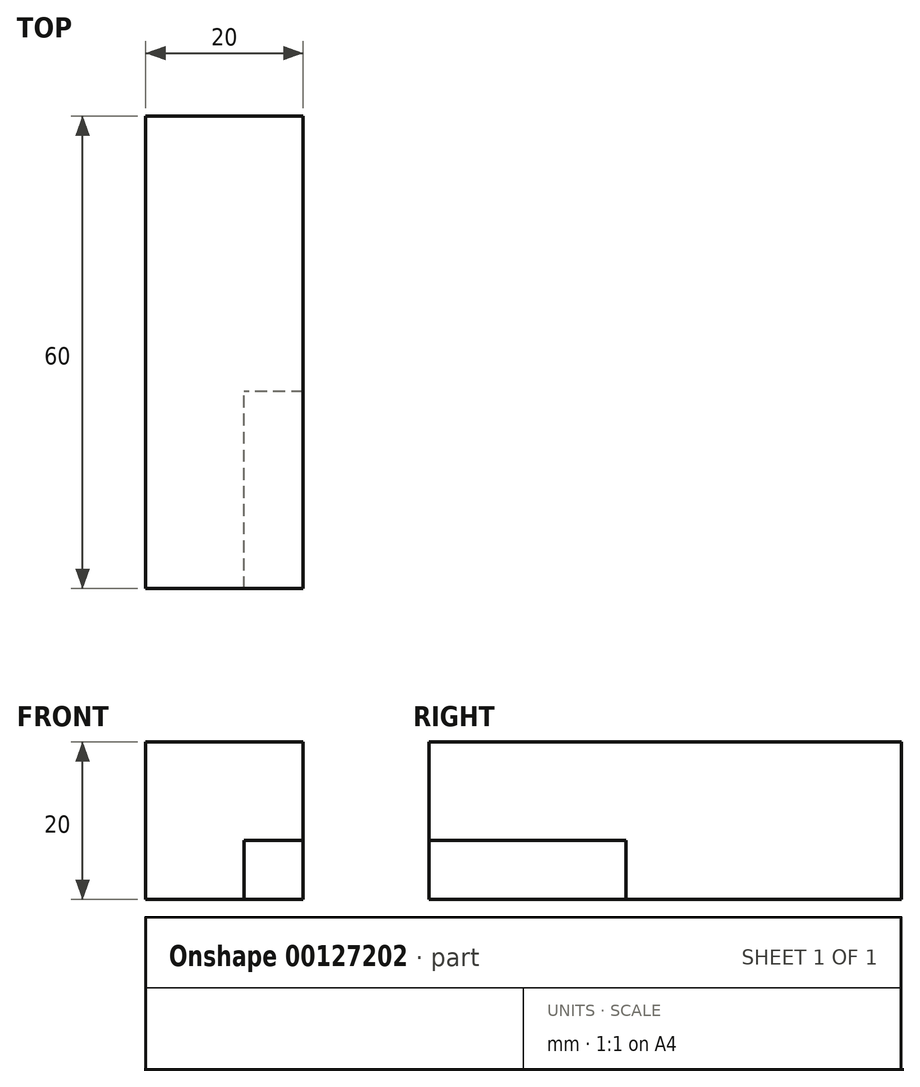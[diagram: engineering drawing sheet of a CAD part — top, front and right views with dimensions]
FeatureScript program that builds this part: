
annotation { "Feature Type Name" : "Feature", "Feature Type Description" : "" }
export const myFeature = defineFeature(function(context is Context, id is Id, definition is map)
    precondition{}
    {
        {
            var Q0;
            Q0=qCreatedBy(makeId("Front.planeOp"),FACE);
            var sketch = newSketch(context, id + "F0", { "sketchPlane" : qUnion([Q0])});
            skLineSegment(sketch, "E0.bottom", {"start": v(-7.5, 0) * mm, "end": v(-20, 0) * mm});
            skLineSegment(sketch, "E0.top", {"start": v(0, 20) * mm, "end": v(-20, 20) * mm});
            skLineSegment(sketch, "E0.left", {"start": v(0, 7.5) * mm, "end": v(0, 20) * mm});
            skLineSegment(sketch, "E0.right", {"start": v(-20, 0) * mm, "end": v(-20, 20) * mm});
            skLineSegment(sketch, "E1.top", {"start": v(0, 7.5) * mm, "end": v(-7.5, 7.5) * mm});
            skLineSegment(sketch, "E1.right", {"start": v(-7.5, 0) * mm, "end": v(-7.5, 7.5) * mm});
            skSolve(sketch);
        }
        {
            var Q0;
            Q0 = qSketchRegion(id + "F0", true);
            extrude(context, id + "F1", {"entities" : qUnion([Q0]), "depth" : 60 * mm});
        }
        {
            var Q0;
            Q0=makeQuery(id+"F1.opExtrude","CAP_FACE",FACE,{"disambiguationData":[OSD([sQuery(id+"F0.wireOp",EDGE,"E0.bottom"),sQuery(id+"F0.wireOp",EDGE,"E0.top"),sQuery(id+"F0.wireOp",EDGE,"E0.left"),sQuery(id+"F0.wireOp",EDGE,"E0.right"),sQuery(id+"F0.wireOp",EDGE,"E1.top"),sQuery(id+"F0.wireOp",EDGE,"E1.right")])],"isStart":true});
            var sketch = newSketch(context, id + "F2", { "sketchPlane" : qUnion([Q0])});
            skLineSegment(sketch, "E2.bottom", {"start": v(0, 7.5) * mm, "end": v(7.5, 7.5) * mm});
            skLineSegment(sketch, "E2.top", {"start": v(0, 0) * mm, "end": v(7.5, 0) * mm});
            skLineSegment(sketch, "E2.left", {"start": v(0, 7.5) * mm, "end": v(0, 0) * mm});
            skLineSegment(sketch, "E2.right", {"start": v(7.5, 7.5) * mm, "end": v(7.5, 0) * mm});
            skSolve(sketch);
        }
        {
            var Q0;
            Q0 = qSketchRegion(id + "F2", true);
            extrude(context, id + "F3", {"entities" : qUnion([Q0]), "operationType" : NewBodyOperationType.ADD, "oppositeDirection" : true, "depth" : 35 * mm});
        }
    });
